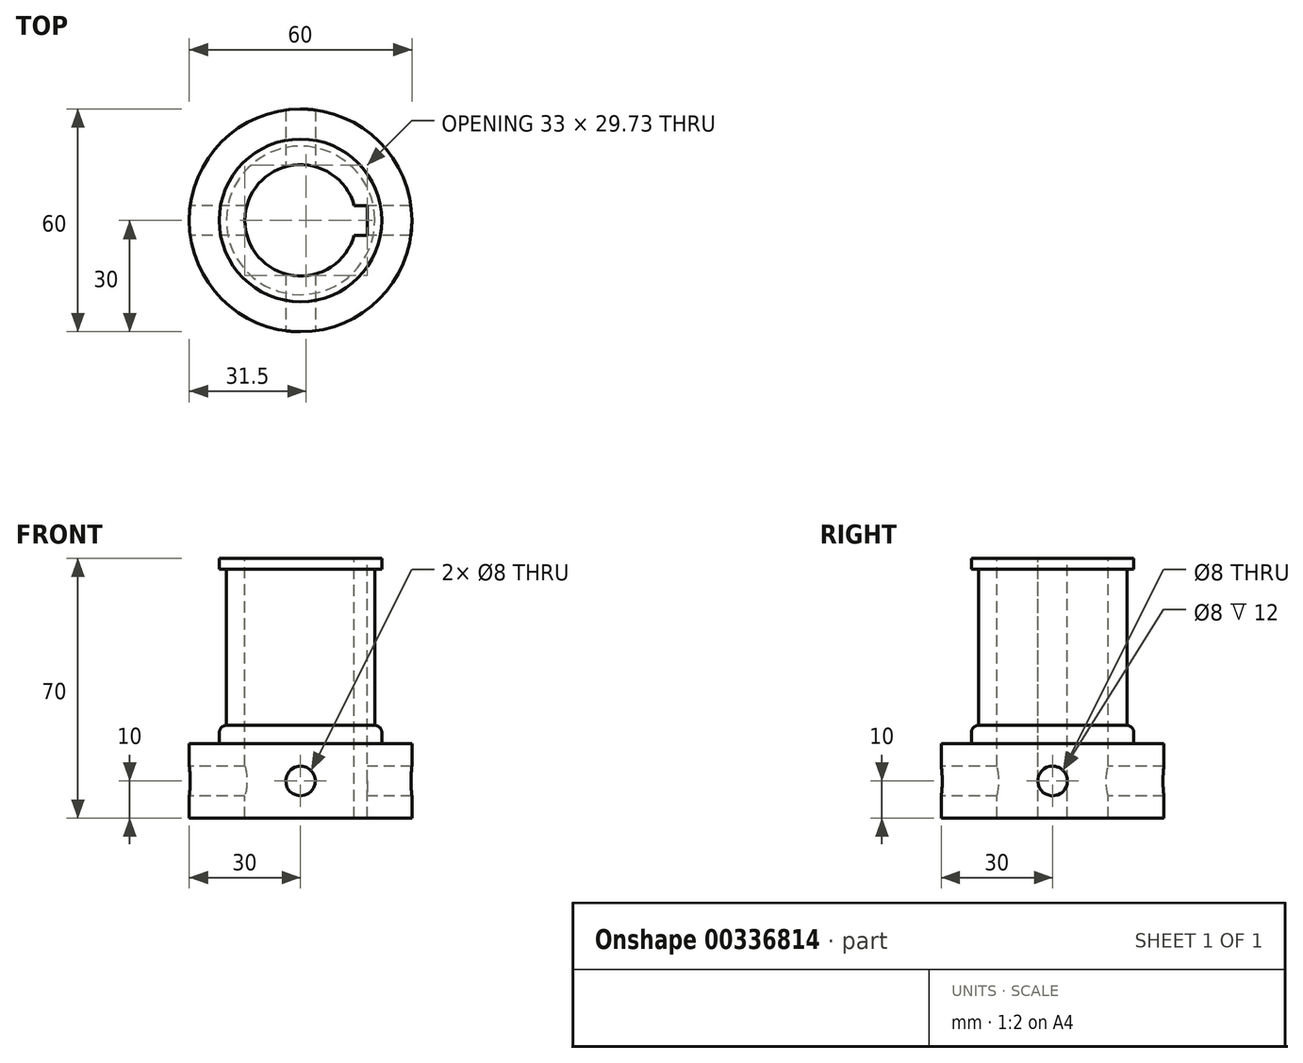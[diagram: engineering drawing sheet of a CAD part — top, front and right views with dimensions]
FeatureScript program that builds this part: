
annotation { "Feature Type Name" : "Feature", "Feature Type Description" : "" }
export const myFeature = defineFeature(function(context is Context, id is Id, definition is map)
    precondition{}
    {
        {
            var Q0;
            Q0=qCreatedBy(makeId("Top.planeOp"),FACE);
            var sketch = newSketch(context, id + "F0", { "sketchPlane" : qUnion([Q0])});
            skCircle(sketch, "E0", {"center": v(0, 0) * mm, "radius": 30 * mm});
            skSolve(sketch);
        }
        {
            var Q0;
            Q0=makeQuery(id+"F0.imprint","IMPRINT",FACE,{"disambiguationData":[TD([[makeQuery(id+"F0.imprint","IMPRINT",EDGE,{"derivedFrom":sQuery(id+"F0.wireOp",EDGE,"E0")}),1.0]])]});
            extrude(context, id + "F1", {"entities" : qUnion([Q0]), "depth" : 20 * mm});
        }
        {
            var Q0;
            Q0=makeQuery(id+"F1.opExtrude","CAP_FACE",FACE,{"disambiguationData":[OSD([sQuery(id+"F0.wireOp",EDGE,"E0")])],"isStart":false});
            var sketch = newSketch(context, id + "F2", { "sketchPlane" : qUnion([Q0])});
            skCircle(sketch, "E1", {"center": v(0, 0) * mm, "radius": 21.9 * mm});
            skSolve(sketch);
        }
        {
            var Q0;
            Q0=makeQuery(id+"F2.imprint","IMPRINT",FACE,{"disambiguationData":[TD([[makeQuery(id+"F2.imprint","IMPRINT",EDGE,{"derivedFrom":sQuery(id+"F2.wireOp",EDGE,"E1")}),1.0]])]});
            extrude(context, id + "F3", {"entities" : qUnion([Q0]), "operationType" : NewBodyOperationType.ADD, "depth" : 5 * mm});
        }
        {
            var Q0;
            Q0=makeQuery(id+"F3.opExtrude","CAP_FACE",FACE,{"disambiguationData":[OSD([sQuery(id+"F2.wireOp",EDGE,"E1")])],"isStart":false});
            var sketch = newSketch(context, id + "F4", { "sketchPlane" : qUnion([Q0])});
            skCircle(sketch, "E2", {"center": v(0, 0) * mm, "radius": 20 * mm});
            skSolve(sketch);
        }
        {
            var Q0;
            Q0=makeQuery(id+"F4.imprint","IMPRINT",FACE,{"disambiguationData":[TD([[makeQuery(id+"F4.imprint","IMPRINT",EDGE,{"derivedFrom":sQuery(id+"F4.wireOp",EDGE,"E2")}),1.0]])]});
            extrude(context, id + "F5", {"entities" : qUnion([Q0]), "operationType" : NewBodyOperationType.ADD, "depth" : 42 * mm});
        }
        {
            var Q0;
            Q0=makeQuery(id+"F5.opExtrude","CAP_FACE",FACE,{"disambiguationData":[OSD([sQuery(id+"F4.wireOp",EDGE,"E2")])],"isStart":false});
            var sketch = newSketch(context, id + "F6", { "sketchPlane" : qUnion([Q0])});
            skCircle(sketch, "E3", {"center": v(0, 0) * mm, "radius": 21.9 * mm});
            skSolve(sketch);
        }
        {
            var Q0;
            Q0 = qSketchRegion(id + "F6", true);
            extrude(context, id + "F7", {"entities" : qUnion([Q0]), "operationType" : NewBodyOperationType.ADD, "depth" : 3 * mm});
        }
        {
            var Q0;
            Q0=makeQuery(id+"F3.opExtrude","CAP_EDGE",EDGE,{"disambiguationData":[OSD([sQuery(id+"F2.wireOp",EDGE,"E1")])],"isStart":false});
            fillet(context, id + "F8", {"entities" : qUnion([Q0]), "radius" : 2 * mm, "tangentPropagation" : true, "allowEdgeOverflow" : false});
        }
        {
            var Q0;
            Q0=makeQuery(id+"F7.opExtrude","CAP_FACE",FACE,{"disambiguationData":[OSD([sQuery(id+"F6.wireOp",EDGE,"E3")])],"isStart":false});
            var sketch = newSketch(context, id + "F9", { "sketchPlane" : qUnion([Q0])});
            skArc(sketch, "E4", {"start": v(14.46, 4) * mm, "mid": v(-15, 0) * mm, "end": v(14.46, -4) * mm});
            skPoint(sketch, "E5", {"position": v(14.46, 4) * mm});
            skPoint(sketch, "E6", {"position": v(14.46, -4) * mm});
            skLineSegment(sketch, "E7", {"start": v(14.46, -4) * mm, "end": v(18, -4) * mm});
            skLineSegment(sketch, "E8", {"start": v(14.46, 4) * mm, "end": v(18, 4) * mm});
            skLineSegment(sketch, "E9", {"start": v(18, -4) * mm, "end": v(18, 4) * mm});
            skPoint(sketch, "E10.end.orphan", {"position": v(18, 0) * mm});
            skLineSegment(sketch, "E11", {"start": v(-15, 0) * mm, "end": v(0, 0) * mm});
            skLineSegment(sketch, "E12", {"start": v(0, 0) * mm, "end": v(15, 0) * mm});
            skLineSegment(sketch, "E13", {"start": v(15, 0) * mm, "end": v(18, 0) * mm});
            skSolve(sketch);
        }
        {
            var Q0;
            Q0=makeQuery(id+"F9.imprint","IMPRINT",FACE,{"disambiguationData":[TD([[makeQuery(id+"F9.imprint","IMPRINT",EDGE,{"derivedFrom":sQuery(id+"F9.wireOp",EDGE,"E4")}),1.0]])]});
            extrude(context, id + "F10", {"entities" : qUnion([Q0]), "operationType" : NewBodyOperationType.REMOVE, "oppositeDirection" : true, "depth" : 75 * mm});
        }
        {
            var Q0;
            Q0=qCreatedBy(makeId("Right.planeOp"),FACE);
            var sketch = newSketch(context, id + "F11", { "sketchPlane" : qUnion([Q0])});
            skLineSegment(sketch, "E14", {"start": v(0, 0) * mm, "end": v(30, 0) * mm});
            skLineSegment(sketch, "E15", {"start": v(30, 0) * mm, "end": v(30, 10) * mm});
            skPoint(sketch, "E16", {"position": v(0, 10) * mm});
            skCircle(sketch, "E17", {"center": v(0, 10) * mm, "radius": 4 * mm});
            skSolve(sketch);
        }
        {
            var Q0;
            Q0 = qSketchRegion(id + "F11", true);
            extrude(context, id + "F12", {"entities" : qUnion([Q0]), "operationType" : NewBodyOperationType.REMOVE, "depth" : 100 * mm, "hasSecondDirection" : true, "secondDirectionOppositeDirection" : true, "secondDirectionDepth" : 100 * mm});
        }
        {
            var Q0;
            Q0=qCreatedBy(makeId("Front.planeOp"),FACE);
            var sketch = newSketch(context, id + "F13", { "sketchPlane" : qUnion([Q0])});
            skLineSegment(sketch, "E18", {"start": v(0, 0) * mm, "end": v(-30, 0) * mm});
            skLineSegment(sketch, "E19", {"start": v(-30, 0) * mm, "end": v(-30, 10) * mm});
            skPoint(sketch, "E20", {"position": v(0, 10) * mm});
            skCircle(sketch, "E21", {"center": v(0, 10) * mm, "radius": 4 * mm});
            skSolve(sketch);
        }
        {
            var Q0;
            Q0 = qSketchRegion(id + "F13", true);
            extrude(context, id + "F14", {"entities" : qUnion([Q0]), "operationType" : NewBodyOperationType.REMOVE, "oppositeDirection" : true, "depth" : 100 * mm, "hasSecondDirection" : true, "secondDirectionOppositeDirection" : false, "secondDirectionDepth" : 100 * mm});
        }
    });
